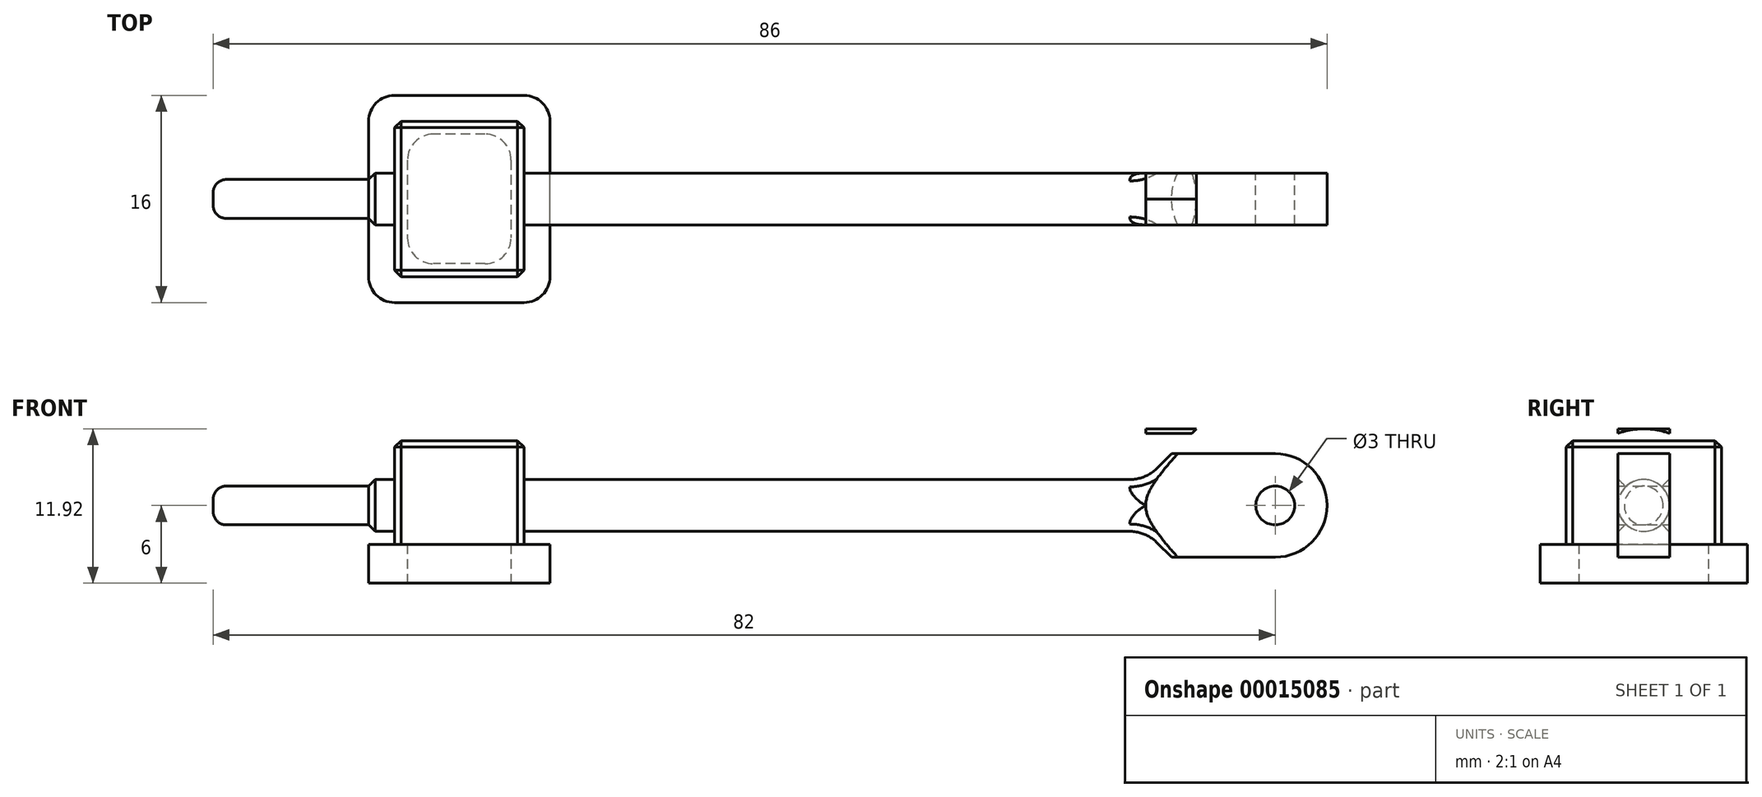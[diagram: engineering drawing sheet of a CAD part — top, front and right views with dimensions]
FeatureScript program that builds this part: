
annotation { "Feature Type Name" : "Feature", "Feature Type Description" : "" }
export const myFeature = defineFeature(function(context is Context, id is Id, definition is map)
    precondition{}
    {
        {
            var Q0;
            Q0=qCreatedBy(makeId("Top.planeOp"),FACE);
            var sketch = newSketch(context, id + "F0", { "sketchPlane" : qUnion([Q0])});
            skLineSegment(sketch, "E0.rect.bottom", {"start": v(7, -8) * mm, "end": v(-7, -8) * mm});
            skLineSegment(sketch, "E0.rect.top", {"start": v(7, 8) * mm, "end": v(-7, 8) * mm});
            skLineSegment(sketch, "E0.rect.left", {"start": v(7, -8) * mm, "end": v(7, 8) * mm});
            skLineSegment(sketch, "E0.rect.right", {"start": v(-7, -8) * mm, "end": v(-7, 8) * mm});
            skPoint(sketch, "E0.rect.middle", {"position": v(0, 0) * mm});
            skSolve(sketch);
        }
        {
            var Q0;
            Q0=makeQuery(id+"F0.imprint","IMPRINT",FACE,{"disambiguationData":[TD([[makeQuery(id+"F0.imprint","IMPRINT",EDGE,{"derivedFrom":sQuery(id+"F0.wireOp",EDGE,"E0.rect.bottom")}),-1.0]])]});
            extrude(context, id + "F1", {"entities" : qUnion([Q0]), "depth" : 3 * mm});
        }
        {
            var Q0;
            Q0=makeQuery(id+"F1.opExtrude","CAP_FACE",FACE,{"disambiguationData":[OSD([sQuery(id+"F0.wireOp",EDGE,"E0.rect.bottom"),sQuery(id+"F0.wireOp",EDGE,"E0.rect.top"),sQuery(id+"F0.wireOp",EDGE,"E0.rect.left"),sQuery(id+"F0.wireOp",EDGE,"E0.rect.right")])],"isStart":false});
            var sketch = newSketch(context, id + "F2", { "sketchPlane" : qUnion([Q0])});
            skLineSegment(sketch, "E1.rect.bottom", {"start": v(5, -6) * mm, "end": v(-5, -6) * mm});
            skLineSegment(sketch, "E1.rect.top", {"start": v(5, 6) * mm, "end": v(-5, 6) * mm});
            skLineSegment(sketch, "E1.rect.left", {"start": v(5, -6) * mm, "end": v(5, 6) * mm});
            skLineSegment(sketch, "E1.rect.right", {"start": v(-5, -6) * mm, "end": v(-5, 6) * mm});
            skPoint(sketch, "E1.rect.middle", {"position": v(0, 0) * mm});
            skSolve(sketch);
        }
        {
            var Q0;
            Q0=makeQuery(id+"F2.imprint","IMPRINT",FACE,{"disambiguationData":[TD([[makeQuery(id+"F2.imprint","IMPRINT",EDGE,{"derivedFrom":sQuery(id+"F2.wireOp",EDGE,"E1.rect.bottom")}),-1.0]])]});
            extrude(context, id + "F3", {"entities" : qUnion([Q0]), "operationType" : NewBodyOperationType.ADD, "depth" : (11 - 3) * mm});
        }
        {
            var Q0;
            Q0=makeQuery(id+"F1.opExtrude","CAP_FACE",FACE,{"disambiguationData":[OSD([sQuery(id+"F0.wireOp",EDGE,"E0.rect.bottom"),sQuery(id+"F0.wireOp",EDGE,"E0.rect.top"),sQuery(id+"F0.wireOp",EDGE,"E0.rect.left"),sQuery(id+"F0.wireOp",EDGE,"E0.rect.right")])],"isStart":true});
            var sketch = newSketch(context, id + "F4", { "sketchPlane" : qUnion([Q0])});
            skLineSegment(sketch, "E2.rect.bottom", {"start": v(4, -5) * mm, "end": v(-4, -5) * mm});
            skLineSegment(sketch, "E2.rect.top", {"start": v(4, 5) * mm, "end": v(-4, 5) * mm});
            skLineSegment(sketch, "E2.rect.left", {"start": v(4, -5) * mm, "end": v(4, 5) * mm});
            skLineSegment(sketch, "E2.rect.right", {"start": v(-4, -5) * mm, "end": v(-4, 5) * mm});
            skPoint(sketch, "E2.rect.middle", {"position": v(0, 0) * mm});
            skSolve(sketch);
        }
        {
            var Q0;
            Q0=makeQuery(id+"F4.imprint","IMPRINT",FACE,{"disambiguationData":[TD([[makeQuery(id+"F4.imprint","IMPRINT",EDGE,{"derivedFrom":sQuery(id+"F4.wireOp",EDGE,"E2.rect.bottom")}),-1.0]])]});
            extrude(context, id + "F5", {"entities" : qUnion([Q0]), "operationType" : NewBodyOperationType.REMOVE, "oppositeDirection" : true, "depth" : 3 * mm});
        }
        {
            var Q0;
            Q0=makeQuery(id+"F3.opExtrude","SWEPT_FACE",FACE,{"disambiguationData":[OSD([sQuery(id+"F2.wireOp",EDGE,"E1.rect.left")])]});
            var sketch = newSketch(context, id + "F6", { "sketchPlane" : qUnion([Q0])});
            skCircle(sketch, "E3", {"center": v(0, 6) * mm, "radius": 2 * mm});
            skSolve(sketch);
        }
        {
            var Q0;
            Q0=makeQuery(id+"F6.imprint","IMPRINT",FACE,{"disambiguationData":[TD([[makeQuery(id+"F6.imprint","IMPRINT",EDGE,{"derivedFrom":sQuery(id+"F6.wireOp",EDGE,"E3")}),1.0]])]});
            extrude(context, id + "F7", {"entities" : qUnion([Q0]), "operationType" : NewBodyOperationType.REMOVE, "endBound" : BoundingType.THROUGH_ALL, "oppositeDirection" : true, "depth" : 25 * mm});
        }
        {
            var Q0;
            Q0=makeQuery(id+"F1.opExtrude","SWEPT_EDGE",EDGE,{"disambiguationData":[OSD([sQuery(id+"F0.wireOp",EDGE,"E0.rect.bottom"),sQuery(id+"F0.wireOp",EDGE,"E0.rect.right")])]});
            var Q1;
            Q1=makeQuery(id+"F1.opExtrude","SWEPT_EDGE",EDGE,{"disambiguationData":[OSD([sQuery(id+"F0.wireOp",EDGE,"E0.rect.top"),sQuery(id+"F0.wireOp",EDGE,"E0.rect.right")])]});
            var Q2;
            Q2=makeQuery(id+"F1.opExtrude","SWEPT_EDGE",EDGE,{"disambiguationData":[OSD([sQuery(id+"F0.wireOp",EDGE,"E0.rect.bottom"),sQuery(id+"F0.wireOp",EDGE,"E0.rect.left")])]});
            var Q3;
            Q3=makeQuery(id+"F1.opExtrude","SWEPT_EDGE",EDGE,{"disambiguationData":[OSD([sQuery(id+"F0.wireOp",EDGE,"E0.rect.top"),sQuery(id+"F0.wireOp",EDGE,"E0.rect.left")])]});
            var Q4;
            Q4=makeQuery(id+"F5.boolean.opBoolean","COPY",EDGE,{"derivedFrom":makeQuery(id+"F5.opExtrude","SWEPT_EDGE",EDGE,{"disambiguationData":[OSD([sQuery(id+"F4.wireOp",EDGE,"E2.rect.top"),sQuery(id+"F4.wireOp",EDGE,"E2.rect.left")])]})});
            var Q5;
            Q5=makeQuery(id+"F5.boolean.opBoolean","COPY",EDGE,{"derivedFrom":makeQuery(id+"F5.opExtrude","SWEPT_EDGE",EDGE,{"disambiguationData":[OSD([sQuery(id+"F4.wireOp",EDGE,"E2.rect.bottom"),sQuery(id+"F4.wireOp",EDGE,"E2.rect.left")])]})});
            var Q6;
            Q6=makeQuery(id+"F5.boolean.opBoolean","COPY",EDGE,{"derivedFrom":makeQuery(id+"F5.opExtrude","SWEPT_EDGE",EDGE,{"disambiguationData":[OSD([sQuery(id+"F4.wireOp",EDGE,"E2.rect.bottom"),sQuery(id+"F4.wireOp",EDGE,"E2.rect.right")])]})});
            var Q7;
            Q7=makeQuery(id+"F5.boolean.opBoolean","COPY",EDGE,{"derivedFrom":makeQuery(id+"F5.opExtrude","SWEPT_EDGE",EDGE,{"disambiguationData":[OSD([sQuery(id+"F4.wireOp",EDGE,"E2.rect.top"),sQuery(id+"F4.wireOp",EDGE,"E2.rect.right")])]})});
            fillet(context, id + "F8", {"entities" : qUnion([Q0, Q1, Q2, Q3, Q4, Q5, Q6, Q7]), "radius" : 2 * mm, "tangentPropagation" : true, "allowEdgeOverflow" : false});
        }
        {
            var Q0;
            Q0=makeQuery(id+"F5.boolean.opBoolean","COPY",EDGE,{"derivedFrom":makeQuery(id+"F5.opExtrude","CAP_EDGE",EDGE,{"disambiguationData":[OSD([sQuery(id+"F4.wireOp",EDGE,"E2.rect.bottom")])],"isStart":true})});
            var Q1;
            Q1=makeQuery(id+"F5.boolean.opBoolean","COPY",EDGE,{"derivedFrom":makeQuery(id+"F5.opExtrude","CAP_EDGE",EDGE,{"disambiguationData":[OSD([sQuery(id+"F4.wireOp",EDGE,"E2.rect.right")])],"isStart":true})});
            var Q2;
            Q2=makeQuery(id+"F5.boolean.opBoolean","COPY",EDGE,{"derivedFrom":makeQuery(id+"F5.opExtrude","CAP_EDGE",EDGE,{"disambiguationData":[OSD([sQuery(id+"F4.wireOp",EDGE,"E2.rect.top")])],"isStart":true})});
            var Q3;
            Q3=makeQuery(id+"F5.boolean.opBoolean","COPY",EDGE,{"derivedFrom":makeQuery(id+"F5.opExtrude","CAP_EDGE",EDGE,{"disambiguationData":[OSD([sQuery(id+"F4.wireOp",EDGE,"E2.rect.left")])],"isStart":true})});
            var Q4;
            Q4=makeQuery(id+"F3.opExtrude","CAP_EDGE",EDGE,{"disambiguationData":[OSD([sQuery(id+"F2.wireOp",EDGE,"E1.rect.bottom")])],"isStart":false});
            var Q5;
            Q5=makeQuery(id+"F3.opExtrude","CAP_EDGE",EDGE,{"disambiguationData":[OSD([sQuery(id+"F2.wireOp",EDGE,"E1.rect.left")])],"isStart":false});
            var Q6;
            Q6=makeQuery(id+"F3.opExtrude","CAP_EDGE",EDGE,{"disambiguationData":[OSD([sQuery(id+"F2.wireOp",EDGE,"E1.rect.top")])],"isStart":false});
            var Q7;
            Q7=makeQuery(id+"F3.opExtrude","CAP_EDGE",EDGE,{"disambiguationData":[OSD([sQuery(id+"F2.wireOp",EDGE,"E1.rect.right")])],"isStart":false});
            var Q8;
            Q8=makeQuery(id+"F3.opExtrude","SWEPT_EDGE",EDGE,{"disambiguationData":[OSD([sQuery(id+"F2.wireOp",EDGE,"E1.rect.top"),sQuery(id+"F2.wireOp",EDGE,"E1.rect.right")])]});
            var Q9;
            Q9=makeQuery(id+"F3.opExtrude","SWEPT_EDGE",EDGE,{"disambiguationData":[OSD([sQuery(id+"F2.wireOp",EDGE,"E1.rect.top"),sQuery(id+"F2.wireOp",EDGE,"E1.rect.left")])]});
            var Q10;
            Q10=makeQuery(id+"F3.opExtrude","SWEPT_EDGE",EDGE,{"disambiguationData":[OSD([sQuery(id+"F2.wireOp",EDGE,"E1.rect.bottom"),sQuery(id+"F2.wireOp",EDGE,"E1.rect.right")])]});
            var Q11;
            Q11=makeQuery(id+"F3.opExtrude","SWEPT_EDGE",EDGE,{"disambiguationData":[OSD([sQuery(id+"F2.wireOp",EDGE,"E1.rect.bottom"),sQuery(id+"F2.wireOp",EDGE,"E1.rect.left")])]});
            chamfer(context, id + "F9", {"entities" : qUnion([Q0, Q1, Q2, Q3, Q4, Q5, Q6, Q7, Q8, Q9, Q10, Q11]), "width" : .5 * mm, "tangentPropagation" : true});
        }
        {
            var Q0;
            Q0=makeQuery(id+"F1.opExtrude","SWEPT_FACE",FACE,{"disambiguationData":[OSD([sQuery(id+"F0.wireOp",EDGE,"E0.rect.right")])]});
            var sketch = newSketch(context, id + "F10", { "sketchPlane" : qUnion([Q0])});
            skCircle(sketch, "E4.0", {"center": v(0, 6) * mm, "radius": 2 * mm});
            skCircle(sketch, "E5", {"center": v(0, 6) * mm, "radius": 1.5 * mm});
            skSolve(sketch);
        }
        {
            var Q0;
            Q0=makeQuery(id+"F10.imprint","IMPRINT",FACE,{"disambiguationData":[TD([[makeQuery(id+"F10.imprint","IMPRINT",EDGE,{"derivedFrom":sQuery(id+"F10.wireOp",EDGE,"E5")}),1.0]])]});
            extrude(context, id + "F11", {"entities" : qUnion([Q0]), "depth" : 12 * mm});
        }
        {
            var Q0;
            Q0=makeQuery(id+"F10.imprint","IMPRINT",FACE,{"disambiguationData":[TD([[makeQuery(id+"F10.imprint","IMPRINT",EDGE,{"derivedFrom":sQuery(id+"F10.wireOp",EDGE,"E5")}),1.0]])]});
            var Q1;
            Q1=makeQuery(id+"F10.imprint","IMPRINT",FACE,{"disambiguationData":[TD([[makeQuery(id+"F10.imprint","IMPRINT",EDGE,{"derivedFrom":sQuery(id+"F10.wireOp",EDGE,"E4.0")}),1.0]])]});
            extrude(context, id + "F12", {"entities" : qUnion([Q0, Q1]), "operationType" : NewBodyOperationType.ADD, "oppositeDirection" : true, "depth" : 60 * mm});
        }
        {
            var Q0;
            Q0=qCreatedBy(makeId("Front.planeOp"),FACE);
            var sketch = newSketch(context, id + "F13", { "sketchPlane" : qUnion([Q0])});
            skLineSegment(sketch, "E6.0", {"start": v(53, 4) * mm, "end": v(53, 8) * mm});
            skLineSegment(sketch, "E7", {"start": v(53, 6) * mm, "end": v(72.65, 6) * mm});
            skLineSegment(sketch, "E8", {"start": v(53, 6) * mm, "end": v(53, 10) * mm});
            skLineSegment(sketch, "E9", {"start": v(53, 10) * mm, "end": v(63, 10) * mm});
            skLineSegment(sketch, "E10", {"start": v(67, 6) * mm, "end": v(67, 6) * mm});
            skLineSegment(sketch, "E11", {"start": v(63, 2) * mm, "end": v(53, 2) * mm});
            skCircle(sketch, "E12", {"center": v(63, 6) * mm, "radius": 1.5 * mm});
            skPoint(sketch, "E13.visualSharp", {"position": v(67, 10) * mm});
            skArc(sketch, "E13.filletArc", {"start": v(67, 6) * mm, "mid": v(65.83, 8.83) * mm, "end": v(63, 10) * mm});
            skPoint(sketch, "E14.visualSharp", {"position": v(67, 2) * mm});
            skArc(sketch, "E14.filletArc", {"start": v(63, 2) * mm, "mid": v(65.83, 3.17) * mm, "end": v(67, 6) * mm});
            skLineSegment(sketch, "E15", {"start": v(-7, 8) * mm, "end": v(53, 8) * mm});
            skLineSegment(sketch, "E16", {"start": v(53, 4) * mm, "end": v(-7, 4) * mm});
            skLineSegment(sketch, "E17", {"start": v(53, 6) * mm, "end": v(53, 2) * mm});
            skLineSegment(sketch, "E18", {"start": v(53, 11.92) * mm, "end": v(53, 6) * mm});
            skLineSegment(sketch, "E19", {"start": v(53, 8) * mm, "end": v(56.92, 11.92) * mm});
            skLineSegment(sketch, "E20", {"start": v(56.92, 11.92) * mm, "end": v(53, 11.92) * mm});
            skSolve(sketch);
        }
        {
            var Q0;
            {var subQ2=sQuery(id+"F13.wireOp",EDGE,"E11");Q0=makeQuery(id+"F13.imprint","IMPRINT",FACE,{"disambiguationData":[TD([[makeQuery(id+"F13.imprint","IMPRINT",EDGE,{"derivedFrom":subQ2}),-1.0]])]});}
            var Q1;
            {var subQ5=sQuery(id+"F13.wireOp",EDGE,"E13.filletArc");Q1=makeQuery(id+"F13.imprint","IMPRINT",FACE,{"disambiguationData":[TD([[makeQuery(id+"F13.imprint","IMPRINT",EDGE,{"derivedFrom":subQ5}),1.0]])]});}
            var Q2;
            {var subQ0=sQuery(id+"F13.wireOp",EDGE,"E18");var subQ1=makeQuery(id+"F13.imprint","IMPRINT",VERTEX,{"derivedFrom":subQ0});Q2=makeQuery(id+"F13.imprint","IMPRINT",FACE,{"disambiguationData":[TD([[makeQuery(id+"F13.imprint","IMPRINT",EDGE,{"disambiguationData":[TD([[subQ1,1.0]])],"derivedFrom":subQ0}),1.0]])]});}
            var Q3;
            {var subQ1=sQuery(id+"F13.wireOp",EDGE,"E9");var subQ3=sQuery(id+"F13.wireOp",EDGE,"E18");var subQ5=makeQuery(id+"F13.imprint","INTERSECT",VERTEX,{"derivedFrom":[subQ1,subQ3]});Q3=makeQuery(id+"F13.imprint","IMPRINT",FACE,{"disambiguationData":[TD([[makeQuery(id+"F13.imprint","IMPRINT",EDGE,{"disambiguationData":[TD([[subQ5,-1.0]])],"derivedFrom":subQ1}),-1.0]])]});}
            extrude(context, id + "F14", {"entities" : qUnion([Q0, Q1, Q2, Q3]), "operationType" : NewBodyOperationType.ADD, "endBound" : BoundingType.SYMMETRIC, "depth" : 4 * mm});
        }
        {
            var Q0;
            {var subQ1=sQuery(id+"F13.wireOp",EDGE,"E9");var subQ3=sQuery(id+"F13.wireOp",EDGE,"E18");var subQ5=makeQuery(id+"F13.imprint","INTERSECT",VERTEX,{"derivedFrom":[subQ1,subQ3]});Q0=makeQuery(id+"F13.imprint","IMPRINT",FACE,{"disambiguationData":[TD([[makeQuery(id+"F13.imprint","IMPRINT",EDGE,{"disambiguationData":[TD([[subQ5,-1.0]])],"derivedFrom":subQ1}),-1.0]])]});}
            var Q1;
            {var subQ0=sQuery(id+"F13.wireOp",EDGE,"E20");Q1=makeQuery(id+"F13.imprint","IMPRINT",FACE,{"disambiguationData":[TD([[makeQuery(id+"F13.imprint","IMPRINT",EDGE,{"derivedFrom":subQ0}),1.0]])]});}
            var Q2;
            Q2=sQuery(id+"F13.wireOp",EDGE,"E7");
            revolve(context, id + "F15", {"operationType" : NewBodyOperationType.REMOVE, "entities" : qUnion([Q0, Q1]), "axis" : qUnion([Q2]), "revolveType" : RevolveType.FULL, "oppositeDirection" : true});
        }
        {
            var Q0;
            Q0=makeQuery(id+"F11.opExtrude","CAP_EDGE",EDGE,{"disambiguationData":[OSD([sQuery(id+"F10.wireOp",EDGE,"E5")])],"isStart":false});
            fillet(context, id + "F16", {"entities" : qUnion([Q0]), "radius" : 1 * mm, "tangentPropagation" : true, "allowEdgeOverflow" : false});
        }
        {
            var Q0;
            Q0=makeQuery(id+"F12.opExtrude","CAP_EDGE",EDGE,{"disambiguationData":[OSD([sQuery(id+"F10.wireOp",EDGE,"E4.0")])],"isStart":true});
            chamfer(context, id + "F17", {"entities" : qUnion([Q0]), "width" : .5 * mm, "tangentPropagation" : true});
        }
        {
            var Q0;
            Q0=makeQuery(id+"F15.boolean.opBoolean","MERGE",EDGE,{"derivedFrom":[makeQuery(id+"F14.boolean.opBoolean","SPLIT",EDGE,{"disambiguationData":[OD(0.0)],"derivedFrom":makeQuery(id+"F12.opExtrude","CAP_EDGE",EDGE,{"disambiguationData":[OSD([sQuery(id+"F10.wireOp",EDGE,"E4.0")])],"isStart":false})}),makeQuery(id+"F15.opRevolve","SWEPT_EDGE",EDGE,{"disambiguationData":[OSD([sQuery(id+"F13.wireOp",EDGE,"E18"),sQuery(id+"F13.wireOp",EDGE,"E19")])]})]});
            fillet(context, id + "F18", {"entities" : qUnion([Q0]), "radius" : 3 * mm, "tangentPropagation" : true, "allowEdgeOverflow" : false});
        }
    });
